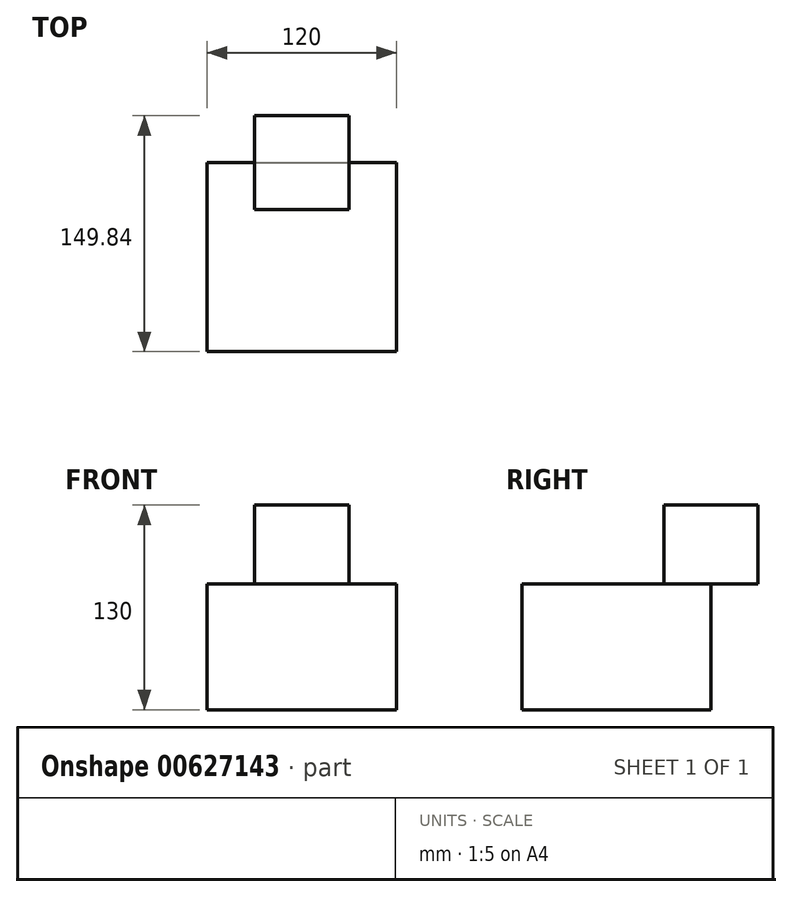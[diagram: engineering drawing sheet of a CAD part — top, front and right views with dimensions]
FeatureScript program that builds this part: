
annotation { "Feature Type Name" : "Feature", "Feature Type Description" : "" }
export const myFeature = defineFeature(function(context is Context, id is Id, definition is map)
    precondition{}
    {
        {
            var Q0;
            Q0=qCreatedBy(makeId("Front.planeOp"),FACE);
            var sketch = newSketch(context, id + "F0", { "sketchPlane" : qUnion([Q0])});
            skLineSegment(sketch, "E0.bottom", {"start": v(-60, 40) * mm, "end": v(60, 40) * mm});
            skLineSegment(sketch, "E0.top", {"start": v(-60, -40) * mm, "end": v(60, -40) * mm});
            skLineSegment(sketch, "E0.left", {"start": v(-60, 40) * mm, "end": v(-60, -40) * mm});
            skLineSegment(sketch, "E0.right", {"start": v(60, 40) * mm, "end": v(60, -40) * mm});
            skPoint(sketch, "E0.middle", {"position": v(0, 0) * mm});
            skSolve(sketch);
        }
        {
            var Q0;
            Q0=makeQuery(id+"F0.imprint","IMPRINT",FACE,{"disambiguationData":[TD([[makeQuery(id+"F0.imprint","IMPRINT",EDGE,{"derivedFrom":sQuery(id+"F0.wireOp",EDGE,"E0.bottom")}),-1.0]])]});
            extrude(context, id + "F1", {"entities" : qUnion([Q0]), "depth" : 120 * mm, "offsetDistance" : 25 * mm});
        }
        {
            var Q0;
            Q0=makeQuery(id+"F1.opExtrude","SWEPT_FACE",FACE,{"disambiguationData":[OSD([sQuery(id+"F0.wireOp",EDGE,"E0.bottom")])]});
            var sketch = newSketch(context, id + "F2", { "sketchPlane" : qUnion([Q0])});
            skLineSegment(sketch, "E1.bottom", {"start": v(-30, 29.84) * mm, "end": v(30, 29.84) * mm});
            skLineSegment(sketch, "E1.top", {"start": v(-30, -29.84) * mm, "end": v(30, -29.84) * mm});
            skLineSegment(sketch, "E1.left", {"start": v(-30, 29.84) * mm, "end": v(-30, -29.84) * mm});
            skLineSegment(sketch, "E1.right", {"start": v(30, 29.84) * mm, "end": v(30, -29.84) * mm});
            skPoint(sketch, "E1.middle", {"position": v(0, 0) * mm});
            skSolve(sketch);
        }
        {
            var Q0;
            Q0 = qSketchRegion(id + "F2", true);
            extrude(context, id + "F3", {"entities" : qUnion([Q0]), "operationType" : NewBodyOperationType.ADD, "depth" : 50 * mm, "offsetDistance" : 25 * mm});
        }
    });
